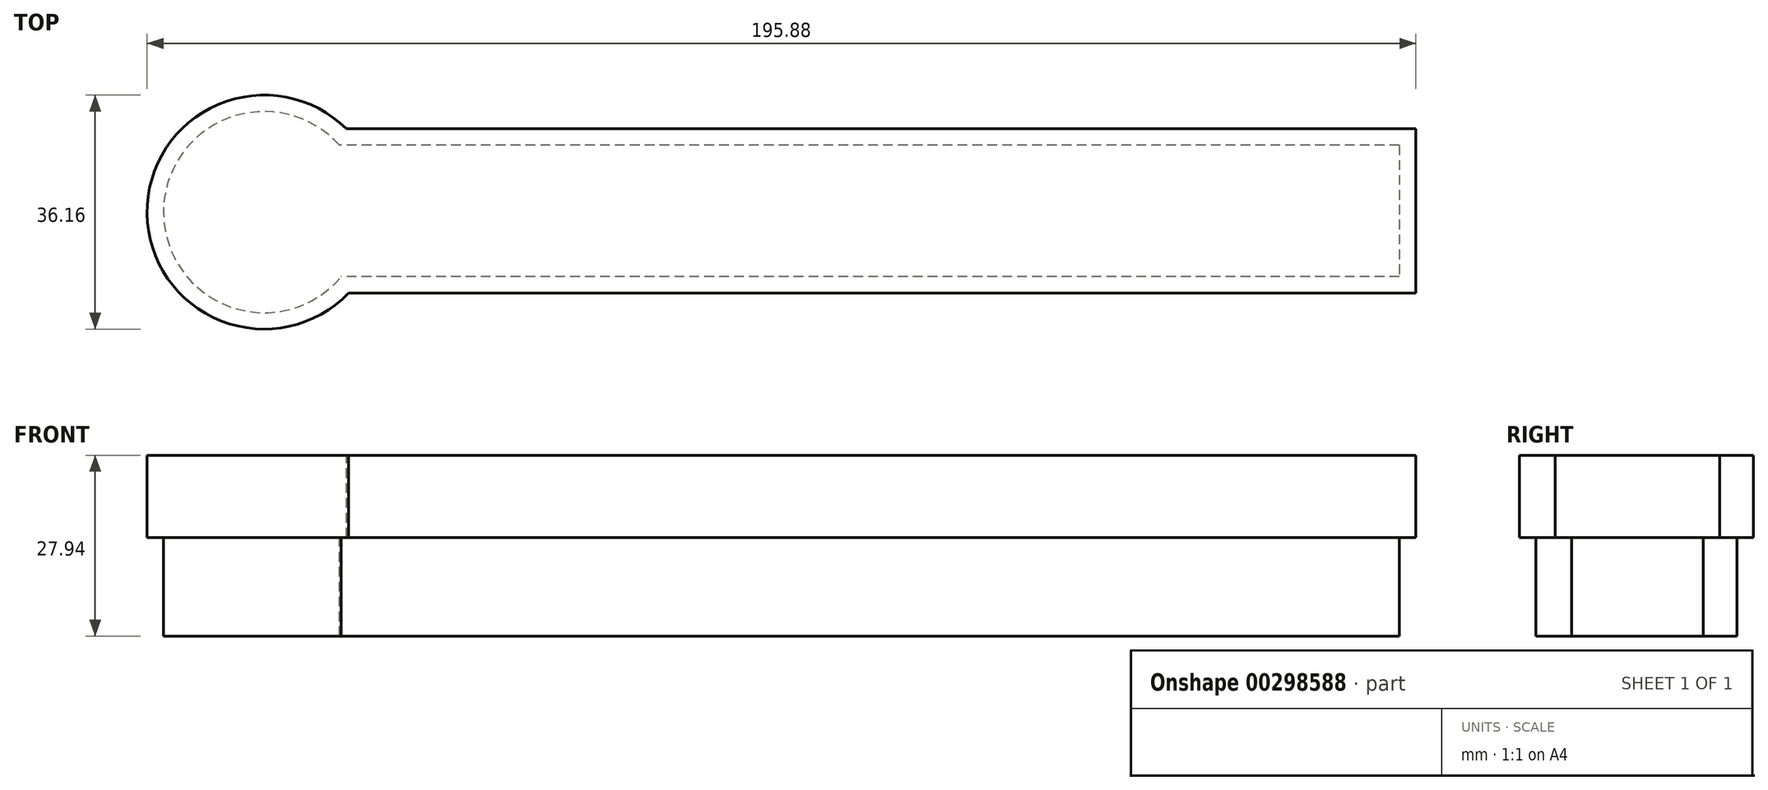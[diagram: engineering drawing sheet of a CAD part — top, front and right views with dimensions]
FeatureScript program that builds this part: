
annotation { "Feature Type Name" : "Feature", "Feature Type Description" : "" }
export const myFeature = defineFeature(function(context is Context, id is Id, definition is map)
    precondition{}
    {
        {
            var Q0;
            Q0=qCreatedBy(makeId("Top.planeOp"),FACE);
            var sketch = newSketch(context, id + "F0", { "sketchPlane" : qUnion([Q0])});
            skLineSegment(sketch, "E0.bottom", {"start": v(0, 12.87) * mm, "end": v(-177.8, 12.87) * mm});
            skLineSegment(sketch, "E0.top", {"start": v(0, -12.53) * mm, "end": v(-177.8, -12.53) * mm});
            skLineSegment(sketch, "E0.left", {"start": v(0, 12.87) * mm, "end": v(0, -12.53) * mm});
            skLineSegment(sketch, "E0.right", {"start": v(-177.8, 12.87) * mm, "end": v(-177.8, -12.53) * mm});
            skCircle(sketch, "E1", {"center": v(-177.8, 0) * mm, "radius": 18.08 * mm});
            skPoint(sketch, "E1.centerSnap0", {"position": v(-177.8, 0.17) * mm});
            skSolve(sketch);
        }
        {
            var Q0;
            Q0 = qSketchRegion(id + "F0", true);
            extrude(context, id + "F1", {"entities" : qUnion([Q0]), "oppositeDirection" : true, "depth" : 12.7 * mm});
        }
        {
            var Q0;
            Q0=makeQuery(id+"F1.opExtrude","CAP_FACE",FACE,{"disambiguationData":[OSD([sQuery(id+"F0.wireOp",EDGE,"E0.bottom"),sQuery(id+"F0.wireOp",EDGE,"E0.top"),sQuery(id+"F0.wireOp",EDGE,"E0.left"),sQuery(id+"F0.wireOp",EDGE,"E1")])],"isStart":false});
            shell(context, id + "F2", {"entities" : qUnion([Q0]), "thickness" : 2.54 * mm});
        }
        {
            var Q0;
            Q0=qCreatedBy(makeId("Front.planeOp"),FACE);
            var sketch = newSketch(context, id + "F3", { "sketchPlane" : qUnion([Q0])});
            skSolve(sketch);
        }
        {
            var Q0;
            Q0 = qSketchRegion(id + "F3", true);
            var Q1;
            Q1=makeQuery(id+"F2.opShell","OFFSET_FACE",FACE,{"disambiguationData":[OSD([sQuery(id+"F0.wireOp",EDGE,"E0.bottom"),sQuery(id+"F0.wireOp",EDGE,"E0.top"),sQuery(id+"F0.wireOp",EDGE,"E0.left"),sQuery(id+"F0.wireOp",EDGE,"E1")])]});
            extrude(context, id + "F4", {"entities" : qUnion([Q0, Q1]), "operationType" : NewBodyOperationType.ADD, "depth" : 25.4 * mm});
        }
    });
